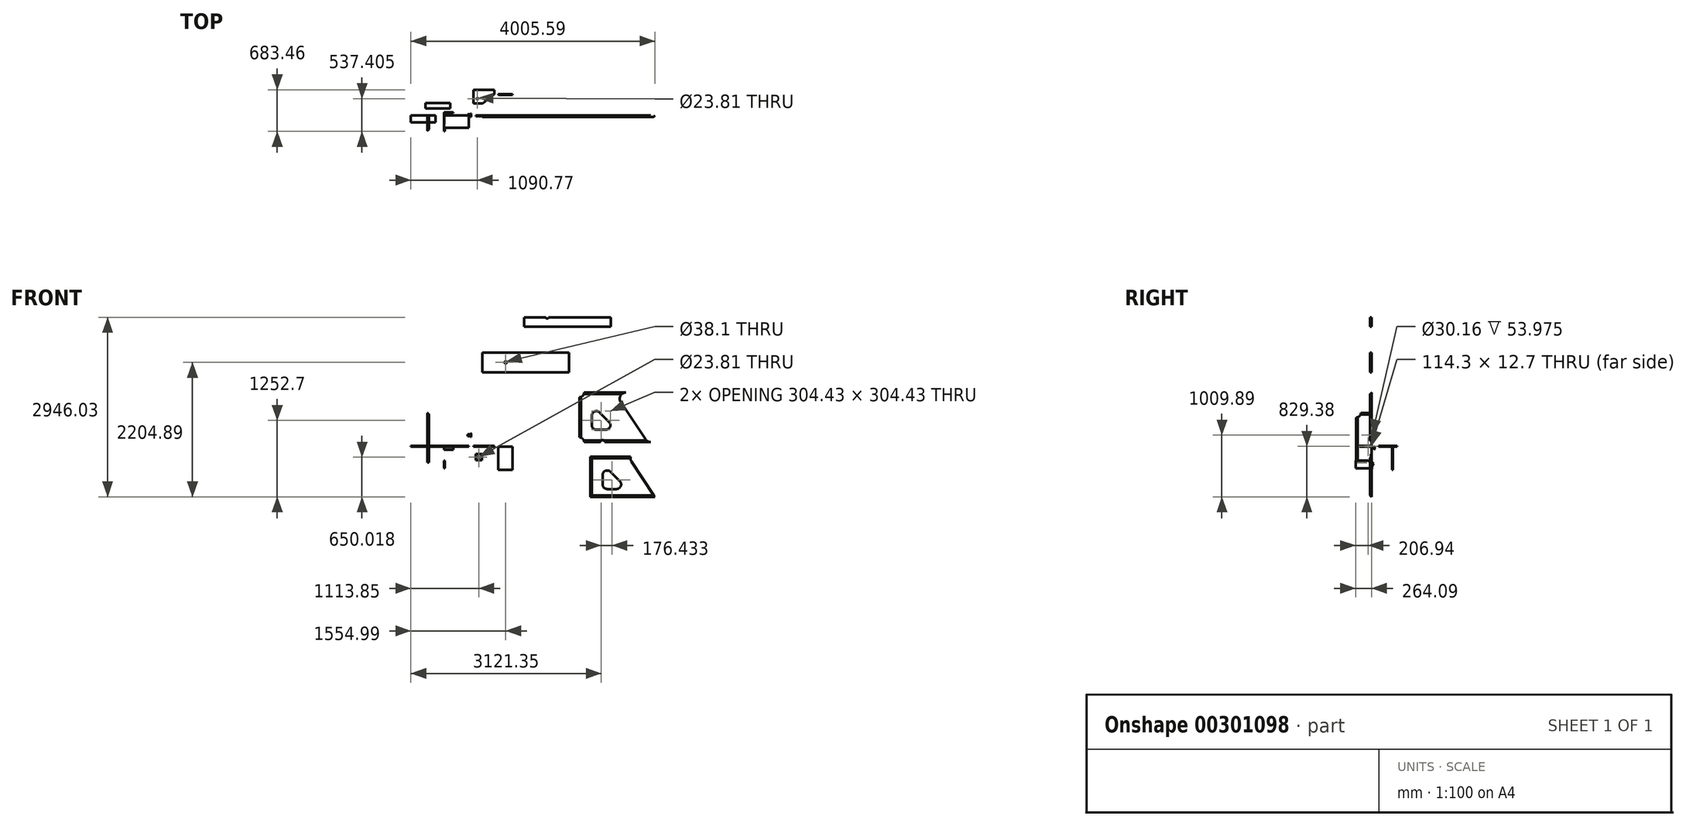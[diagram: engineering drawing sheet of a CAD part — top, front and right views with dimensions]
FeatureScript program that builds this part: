
annotation { "Feature Type Name" : "Feature", "Feature Type Description" : "" }
export const myFeature = defineFeature(function(context is Context, id is Id, definition is map)
    precondition{}
    {
        {
            var Q0;
            Q0=qCreatedBy(makeId("Top.planeOp"),FACE);
            var sketch = newSketch(context, id + "F0", { "sketchPlane" : qUnion([Q0])});
            skLineSegment(sketch, "E0.bottom", {"start": v(0, 0) * mm, "end": v(406.4, 0) * mm});
            skLineSegment(sketch, "E0.top", {"start": v(0, -203.2) * mm, "end": v(406.4, -203.2) * mm});
            skLineSegment(sketch, "E0.left", {"start": v(0, 0) * mm, "end": v(0, -203.2) * mm});
            skLineSegment(sketch, "E0.right", {"start": v(406.4, 0) * mm, "end": v(406.4, -203.2) * mm});
            skSolve(sketch);
        }
        {
            var Q0;
            Q0=makeQuery(id+"F0.imprint","IMPRINT",FACE,{"disambiguationData":[TD([[makeQuery(id+"F0.imprint","IMPRINT",EDGE,{"derivedFrom":sQuery(id+"F0.wireOp",EDGE,"E0.bottom")}),-1.0]])]});
            extrude(context, id + "F1", {"entities" : qUnion([Q0]), "depth" : 12.7 * mm});
        }
        {
            var Q0;
            Q0=makeQuery(id+"F1.opExtrude","SWEPT_FACE",FACE,{"disambiguationData":[OSD([sQuery(id+"F0.wireOp",EDGE,"E0.left")])]});
            var sketch = newSketch(context, id + "F2", { "sketchPlane" : qUnion([Q0])});
            skLineSegment(sketch, "E1", {"start": v(203.2, 12.7) * mm, "end": v(203.2, 0) * mm});
            skLineSegment(sketch, "E2", {"start": v(203.2, 0) * mm, "end": v(199.8, 0) * mm});
            skLineSegment(sketch, "E3", {"start": v(199.8, 0) * mm, "end": v(203.2, 12.7) * mm});
            skSolve(sketch);
        }
        {
            var Q0;
            Q0 = qSketchRegion(id + "F2", true);
            var Q1;
            Q1=makeQuery(id+"F1.opExtrude","SWEPT_BODY",BODY,{"disambiguationData":[OSD([sQuery(id+"F0.wireOp",EDGE,"E0.bottom"),sQuery(id+"F0.wireOp",EDGE,"E0.top"),sQuery(id+"F0.wireOp",EDGE,"E0.left"),sQuery(id+"F0.wireOp",EDGE,"E0.right")])]});
            extrude(context, id + "F3", {"entities" : qUnion([Q0]), "operationType" : NewBodyOperationType.REMOVE, "endBound" : BoundingType.UP_TO_BODY, "oppositeDirection" : true, "endBoundEntityBody" : qUnion([Q1]), "depth" : 25.4 * mm});
        }
        {
            var Q0;
            Q0=qCreatedBy(makeId("Top.planeOp"),FACE);
            var sketch = newSketch(context, id + "F4", { "sketchPlane" : qUnion([Q0])});
            skLineSegment(sketch, "E4.bottom", {"start": v(-140.72, 0) * mm, "end": v(-547.12, 0) * mm});
            skLineSegment(sketch, "E4.top", {"start": v(-140.72, -114.3) * mm, "end": v(-547.12, -114.3) * mm});
            skLineSegment(sketch, "E4.left", {"start": v(-140.72, 0) * mm, "end": v(-140.72, -114.3) * mm});
            skLineSegment(sketch, "E4.right", {"start": v(-547.12, 0) * mm, "end": v(-547.12, -114.3) * mm});
            skSolve(sketch);
        }
        {
            var Q0;
            Q0=makeQuery(id+"F4.imprint","IMPRINT",FACE,{"disambiguationData":[TD([[makeQuery(id+"F4.imprint","IMPRINT",EDGE,{"derivedFrom":sQuery(id+"F4.wireOp",EDGE,"E4.bottom")}),1.0]])]});
            extrude(context, id + "F5", {"entities" : qUnion([Q0]), "depth" : 12.7 * mm});
        }
        {
            var Q0;
            Q0=makeQuery(id+"F5.opExtrude","SWEPT_FACE",FACE,{"disambiguationData":[OSD([sQuery(id+"F4.wireOp",EDGE,"E4.right")])]});
            var sketch = newSketch(context, id + "F6", { "sketchPlane" : qUnion([Q0])});
            skLineSegment(sketch, "E5", {"start": v(0, 12.7) * mm, "end": v(0, 0) * mm});
            skLineSegment(sketch, "E6", {"start": v(0, 0) * mm, "end": v(3.4, 0) * mm});
            skLineSegment(sketch, "E7", {"start": v(3.4, 0) * mm, "end": v(0, 12.7) * mm});
            skSolve(sketch);
        }
        {
            var Q0;
            Q0 = qSketchRegion(id + "F6", true);
            extrude(context, id + "F7", {"entities" : qUnion([Q0]), "operationType" : NewBodyOperationType.REMOVE, "endBound" : BoundingType.THROUGH_ALL, "oppositeDirection" : true, "depth" : 25.4 * mm});
        }
        {
            var Q0;
            Q0=qCreatedBy(makeId("Top.planeOp"),FACE);
            var sketch = newSketch(context, id + "F8", { "sketchPlane" : qUnion([Q0])});
            skLineSegment(sketch, "E8.bottom", {"start": v(-305.25, 203.53) * mm, "end": v(101.15, 203.53) * mm});
            skLineSegment(sketch, "E8.top", {"start": v(-305.25, 114.63) * mm, "end": v(101.15, 114.63) * mm});
            skLineSegment(sketch, "E8.left", {"start": v(-305.25, 203.53) * mm, "end": v(-305.25, 114.63) * mm});
            skLineSegment(sketch, "E8.right", {"start": v(101.15, 203.53) * mm, "end": v(101.15, 114.63) * mm});
            skSolve(sketch);
        }
        {
            var Q0;
            Q0=makeQuery(id+"F8.imprint","IMPRINT",FACE,{"disambiguationData":[TD([[makeQuery(id+"F8.imprint","IMPRINT",EDGE,{"derivedFrom":sQuery(id+"F8.wireOp",EDGE,"E8.bottom")}),-1.0]])]});
            extrude(context, id + "F9", {"entities" : qUnion([Q0]), "depth" : 12.7 * mm});
        }
        {
            var Q0;
            Q0=qCreatedBy(makeId("Right.planeOp"),FACE);
            var sketch = newSketch(context, id + "F10", { "sketchPlane" : qUnion([Q0])});
            skLineSegment(sketch, "E9", {"start": v(-264.09, -226.14) * mm, "end": v(-64.29, -226.14) * mm});
            skLineSegment(sketch, "E10", {"start": v(-64.29, -226.14) * mm, "end": v(31.75, -281.59) * mm});
            skLineSegment(sketch, "E11", {"start": v(31.75, -281.59) * mm, "end": v(0, -336.58) * mm});
            skLineSegment(sketch, "E12", {"start": v(0, -336.58) * mm, "end": v(11, -342.93) * mm});
            skLineSegment(sketch, "E13", {"start": v(11, -342.93) * mm, "end": v(4.65, -353.93) * mm});
            skLineSegment(sketch, "E14", {"start": v(4.65, -353.93) * mm, "end": v(-264.09, -353.93) * mm});
            skLineSegment(sketch, "E15", {"start": v(-264.09, -353.93) * mm, "end": v(-264.09, -226.14) * mm});
            skSolve(sketch);
        }
        {
            var Q0;
            Q0=makeQuery(id+"F10.imprint","IMPRINT",FACE,{"disambiguationData":[TD([[makeQuery(id+"F10.imprint","IMPRINT",EDGE,{"derivedFrom":sQuery(id+"F10.wireOp",EDGE,"E9")}),-1.0]])]});
            extrude(context, id + "F11", {"entities" : qUnion([Q0]), "depth" : 12.7 * mm});
        }
        {
            var Q0;
            Q0=qCreatedBy(makeId("Right.planeOp"),FACE);
            var sketch = newSketch(context, id + "F12", { "sketchPlane" : qUnion([Q0])});
            skLineSegment(sketch, "E16.bottom", {"start": v(50.16, 0) * mm, "end": v(37.46, 0) * mm});
            skLineSegment(sketch, "E16.left", {"start": v(50.16, 0) * mm, "end": v(50.16, -38.1) * mm});
            skLineSegment(sketch, "E16.right", {"start": v(37.46, 0) * mm, "end": v(37.46, -50.8) * mm});
            skLineSegment(sketch, "E17", {"start": v(37.46, -50.8) * mm, "end": v(50.16, -38.1) * mm});
            skSolve(sketch);
        }
        {
            var Q0;
            Q0 = qSketchRegion(id + "F12", true);
            extrude(context, id + "F13", {"entities" : qUnion([Q0]), "depth" : 152.4 * mm});
        }
        {
            var Q0;
            Q0=qCreatedBy(makeId("Front.planeOp"),FACE);
            var sketch = newSketch(context, id + "F14", { "sketchPlane" : qUnion([Q0])});
            skLineSegment(sketch, "E18.bottom", {"start": v(-274.81, 553.7) * mm, "end": v(-249.41, 553.7) * mm});
            skLineSegment(sketch, "E18.top", {"start": v(-274.81, -259.1) * mm, "end": v(-249.41, -259.1) * mm});
            skLineSegment(sketch, "E18.left", {"start": v(-274.81, 553.7) * mm, "end": v(-274.81, -259.1) * mm});
            skLineSegment(sketch, "E18.right", {"start": v(-249.41, 553.7) * mm, "end": v(-249.41, -259.1) * mm});
            skSolve(sketch);
        }
        {
            var Q0;
            Q0 = qSketchRegion(id + "F14", true);
            extrude(context, id + "F15", {"entities" : qUnion([Q0]), "operationType" : NewBodyOperationType.ADD, "depth" : 254 * mm});
        }
        {
            var Q0;
            Q0=makeQuery(id+"F15.opExtrude","SWEPT_FACE",FACE,{"disambiguationData":[OSD([sQuery(id+"F14.wireOp",EDGE,"E18.right")])]});
            var sketch = newSketch(context, id + "F16", { "sketchPlane" : qUnion([Q0])});
            skCircle(sketch, "E19", {"center": v(-254, 553.7) * mm, "radius": 76.2 * mm});
            skSolve(sketch);
        }
        {
            var Q0;
            Q0 = qSketchRegion(id + "F16", true);
            extrude(context, id + "F17", {"entities" : qUnion([Q0]), "operationType" : NewBodyOperationType.REMOVE, "oppositeDirection" : true, "depth" : 25.4 * mm});
        }
        {
            var Q0;
            Q0=makeQuery(id+"F15.opExtrude","CAP_FACE",FACE,{"disambiguationData":[OSD([sQuery(id+"F14.wireOp",EDGE,"E18.bottom"),sQuery(id+"F14.wireOp",EDGE,"E18.top"),sQuery(id+"F14.wireOp",EDGE,"E18.left"),sQuery(id+"F14.wireOp",EDGE,"E18.right")])],"isStart":true});
            var sketch = newSketch(context, id + "F18", { "sketchPlane" : qUnion([Q0])});
            skLineSegment(sketch, "E20", {"start": v(274.81, 553.7) * mm, "end": v(249.41, 553.7) * mm});
            skLineSegment(sketch, "E21", {"start": v(249.41, 553.7) * mm, "end": v(249.41, 528.3) * mm});
            skLineSegment(sketch, "E22", {"start": v(249.41, 528.3) * mm, "end": v(274.81, 553.7) * mm});
            skSolve(sketch);
        }
        {
            var Q0;
            Q0 = qSketchRegion(id + "F18", true);
            extrude(context, id + "F19", {"entities" : qUnion([Q0]), "operationType" : NewBodyOperationType.REMOVE, "endBound" : BoundingType.UP_TO_NEXT, "oppositeDirection" : true, "depth" : 25.4 * mm});
        }
        {
            var Q0;
            Q0=makeQuery(id+"F15.opExtrude","SWEPT_FACE",FACE,{"disambiguationData":[OSD([sQuery(id+"F14.wireOp",EDGE,"E18.top")])]});
            var sketch = newSketch(context, id + "F20", { "sketchPlane" : qUnion([Q0])});
            skLineSegment(sketch, "E23", {"start": v(-274.81, 254) * mm, "end": v(-249.41, 254) * mm});
            skLineSegment(sketch, "E24", {"start": v(-249.41, 254) * mm, "end": v(-249.41, 228.6) * mm});
            skLineSegment(sketch, "E25", {"start": v(-249.41, 228.6) * mm, "end": v(-274.81, 254) * mm});
            skSolve(sketch);
        }
        {
            var Q0;
            Q0 = qSketchRegion(id + "F20", true);
            extrude(context, id + "F21", {"entities" : qUnion([Q0]), "operationType" : NewBodyOperationType.REMOVE, "endBound" : BoundingType.UP_TO_NEXT, "oppositeDirection" : true, "depth" : 25.4 * mm});
        }
        {
            var Q0;
            Q0=qCreatedBy(makeId("Front.planeOp"),FACE);
            var sketch = newSketch(context, id + "F22", { "sketchPlane" : qUnion([Q0])});
            skLineSegment(sketch, "E26", {"start": v(384.29, 203.53) * mm, "end": v(435.09, 203.53) * mm});
            skLineSegment(sketch, "E27", {"start": v(435.09, 203.53) * mm, "end": v(435.09, 215.44) * mm});
            skLineSegment(sketch, "E28", {"start": v(435.09, 215.44) * mm, "end": v(438.26, 215.44) * mm});
            skLineSegment(sketch, "E29", {"start": v(438.26, 215.44) * mm, "end": v(438.26, 201.95) * mm});
            skLineSegment(sketch, "E30", {"start": v(438.26, 201.95) * mm, "end": v(384.29, 201.95) * mm});
            skLineSegment(sketch, "E31", {"start": v(384.29, 201.95) * mm, "end": v(384.29, 203.53) * mm});
            skLineSegment(sketch, "E32", {"start": v(375.4, 186.86) * mm, "end": v(470.53, 186.86) * mm});
            skSolve(sketch);
        }
        {
            var Q0;
            Q0=makeQuery(id+"F22.imprint","IMPRINT",FACE,{"disambiguationData":[TD([[makeQuery(id+"F22.imprint","IMPRINT",EDGE,{"derivedFrom":sQuery(id+"F22.wireOp",EDGE,"E26")}),-1.0]])]});
            var Q1;
            Q1=sQuery(id+"F22.wireOp",EDGE,"E32");
            revolve(context, id + "F23", {"entities" : qUnion([Q0]), "axis" : qUnion([Q1]), "revolveType" : RevolveType.FULL});
        }
        {
            var Q0;
            Q0=qCreatedBy(makeId("Top.planeOp"),FACE);
            var sketch = newSketch(context, id + "F24", { "sketchPlane" : qUnion([Q0])});
            skLineSegment(sketch, "E33", {"start": v(480.15, 419.37) * mm, "end": v(823.05, 419.37) * mm});
            skLineSegment(sketch, "E34", {"start": v(823.05, 419.37) * mm, "end": v(823.05, 352.7) * mm});
            skLineSegment(sketch, "E35", {"start": v(820.67, 347.73) * mm, "end": v(632.55, 197.12) * mm});
            skLineSegment(sketch, "E36", {"start": v(632.55, 197.12) * mm, "end": v(480.15, 197.12) * mm});
            skLineSegment(sketch, "E37", {"start": v(480.15, 197.12) * mm, "end": v(480.15, 419.37) * mm});
            skPoint(sketch, "E38.visualSharp", {"position": v(823.05, 349.64) * mm});
            skArc(sketch, "E38.filletArc", {"start": v(820.67, 347.73) * mm, "mid": v(822.43, 349.94) * mm, "end": v(823.05, 352.7) * mm});
            skCircle(sketch, "E39", {"center": v(543.65, 273.32) * mm, "radius": 11.9 * mm});
            skSolve(sketch);
        }
        {
            var Q0;
            Q0 = qSketchRegion(id + "F24", true);
            extrude(context, id + "F25", {"entities" : qUnion([Q0]), "depth" : 12.7 * mm});
        }
        {
            var Q0;
            Q0=qCreatedBy(makeId("Top.planeOp"),FACE);
            var sketch = newSketch(context, id + "F26", { "sketchPlane" : qUnion([Q0])});
            skLineSegment(sketch, "E40.bottom", {"start": v(1123.97, 349.32) * mm, "end": v(888.39, 349.32) * mm});
            skLineSegment(sketch, "E40.top", {"start": v(1123.97, 336.62) * mm, "end": v(894.74, 336.62) * mm});
            skLineSegment(sketch, "E40.left", {"start": v(1123.97, 349.32) * mm, "end": v(1123.97, 336.62) * mm});
            skLineSegment(sketch, "E40.right", {"start": v(888.39, 349.32) * mm, "end": v(888.39, 342.97) * mm});
            skPoint(sketch, "E41.visualSharp", {"position": v(888.39, 336.62) * mm});
            skArc(sketch, "E41.filletArc", {"start": v(888.39, 342.97) * mm, "mid": v(890.25, 338.48) * mm, "end": v(894.74, 336.62) * mm});
            skSolve(sketch);
        }
        {
            var Q0;
            Q0 = qSketchRegion(id + "F26", true);
            extrude(context, id + "F27", {"entities" : qUnion([Q0]), "oppositeDirection" : true, "depth" : 381 * mm});
        }
        {
            var Q0;
            Q0=qCreatedBy(makeId("Front.planeOp"),FACE);
            var sketch = newSketch(context, id + "F28", { "sketchPlane" : qUnion([Q0])});
            skLineSegment(sketch, "E42.bottom", {"start": v(515.93, -122.21) * mm, "end": v(617.53, -122.21) * mm});
            skLineSegment(sketch, "E42.top", {"start": v(515.93, -223.81) * mm, "end": v(617.53, -223.81) * mm});
            skLineSegment(sketch, "E42.left", {"start": v(515.93, -122.21) * mm, "end": v(515.93, -223.81) * mm});
            skLineSegment(sketch, "E42.right", {"start": v(617.53, -122.21) * mm, "end": v(617.53, -223.81) * mm});
            skCircle(sketch, "E43", {"center": v(566.73, -173.01) * mm, "radius": 11.9 * mm});
            skSolve(sketch);
        }
        {
            var Q0;
            Q0 = qSketchRegion(id + "F28", true);
            extrude(context, id + "F29", {"entities" : qUnion([Q0]), "depth" : 12.7 * mm});
        }
        {
            var Q0;
            Q0=qCreatedBy(makeId("Front.planeOp"),FACE);
            var sketch = newSketch(context, id + "F30", { "sketchPlane" : qUnion([Q0])});
            skLineSegment(sketch, "E44.bottom", {"start": v(626.87, 1543.77) * mm, "end": v(2049.27, 1543.77) * mm});
            skLineSegment(sketch, "E44.top", {"start": v(626.87, 1219.95) * mm, "end": v(2049.27, 1219.95) * mm});
            skLineSegment(sketch, "E44.left", {"start": v(626.87, 1543.77) * mm, "end": v(626.87, 1219.95) * mm});
            skLineSegment(sketch, "E44.right", {"start": v(2049.27, 1543.77) * mm, "end": v(2049.27, 1219.95) * mm});
            skCircle(sketch, "E45", {"center": v(1007.87, 1381.86) * mm, "radius": 19.05 * mm});
            skLineSegment(sketch, "E46.bottom", {"start": v(1308.62, 2123) * mm, "end": v(1667.4, 2123) * mm});
            skLineSegment(sketch, "E46.left", {"start": v(1308.62, 2123) * mm, "end": v(1308.62, 1970.6) * mm});
            skLineSegment(sketch, "E46.right", {"start": v(2731.02, 2123) * mm, "end": v(2731.02, 1970.6) * mm});
            skLineSegment(sketch, "E47", {"start": v(2218.81, 810.85) * mm, "end": v(2218.81, 150.45) * mm});
            skLineSegment(sketch, "E48", {"start": v(2295.01, 74.25) * mm, "end": v(2564.89, 74.25) * mm});
            skLineSegment(sketch, "E49", {"start": v(2295.01, 887.05) * mm, "end": v(2980.81, 887.05) * mm});
            skLineSegment(sketch, "E50", {"start": v(2980.81, 887.05) * mm, "end": v(2980.81, 887.05) * mm});
            skArc(sketch, "E51", {"start": v(2218.81, 810.85) * mm, "mid": v(2272.7, 833.17) * mm, "end": v(2295.01, 887.05) * mm});
            skArc(sketch, "E52", {"start": v(2295.01, 74.25) * mm, "mid": v(2272.7, 128.13) * mm, "end": v(2218.81, 150.45) * mm});
            skArc(sketch, "E53", {"start": v(2552.1, 559.93) * mm, "mid": v(2469.05, 576.45) * mm, "end": v(2422.01, 506.05) * mm});
            skArc(sketch, "E54", {"start": v(2422.01, 353.65) * mm, "mid": v(2444.33, 299.77) * mm, "end": v(2498.21, 277.45) * mm});
            skArc(sketch, "E55", {"start": v(2650.61, 277.45) * mm, "mid": v(2721.01, 324.5) * mm, "end": v(2704.5, 407.53) * mm});
            skLineSegment(sketch, "E56", {"start": v(2498.21, 277.45) * mm, "end": v(2650.61, 277.45) * mm});
            skLineSegment(sketch, "E57", {"start": v(2422.01, 506.05) * mm, "end": v(2422.01, 353.65) * mm});
            skLineSegment(sketch, "E58", {"start": v(2552.1, 559.93) * mm, "end": v(2704.5, 407.53) * mm});
            skLineSegment(sketch, "E59.right", {"start": v(3302.68, 233.8) * mm, "end": v(3302.68, 232.2) * mm});
            skLineSegment(sketch, "E60", {"start": v(2896.28, 729.1) * mm, "end": v(3302.68, 119.5) * mm});
            skArc(sketch, "E61", {"start": v(3302.68, 119.5) * mm, "mid": v(3339.27, 86.27) * mm, "end": v(3387.21, 74.25) * mm});
            skArc(sketch, "E62", {"start": v(2980.81, 887.05) * mm, "mid": v(2891.24, 833.4) * mm, "end": v(2896.28, 729.1) * mm});
            skPoint(sketch, "E63", {"position": v(1308.62, 2046.8) * mm});
            skPoint(sketch, "E64", {"position": v(626.87, 1381.86) * mm});
            skArc(sketch, "E65", {"start": v(2634.74, 74.25) * mm, "mid": v(2599.81, 109.18) * mm, "end": v(2564.89, 74.25) * mm});
            skLineSegment(sketch, "E66.trimOffspring", {"start": v(2634.74, 74.25) * mm, "end": v(3387.21, 74.25) * mm});
            skLineSegment(sketch, "E67.trimOffspring", {"start": v(1308.62, 1970.6) * mm, "end": v(2731.02, 1970.6) * mm});
            skArc(sketch, "E68", {"start": v(1667.4, 2123) * mm, "mid": v(1689.62, 2100.77) * mm, "end": v(1711.85, 2123) * mm});
            skLineSegment(sketch, "E69.trimOffspring", {"start": v(1711.85, 2123) * mm, "end": v(2731.02, 2123) * mm});
            skSolve(sketch);
        }
        {
            var Q0;
            Q0 = qSketchRegion(id + "F30", true);
            extrude(context, id + "F31", {"entities" : qUnion([Q0]), "depth" : 25.4 * mm});
        }
        {
            var Q0;
            Q0=makeQuery(id+"F31.opExtrude","CAP_EDGE",EDGE,{"disambiguationData":[OSD([sQuery(id+"F30.wireOp",EDGE,"E49")])],"isStart":false});
            var Q1;
            Q1=makeQuery(id+"F31.opExtrude","CAP_EDGE",EDGE,{"disambiguationData":[OSD([sQuery(id+"F30.wireOp",EDGE,"E48")])],"isStart":false});
            var Q2;
            Q2=makeQuery(id+"F31.opExtrude","CAP_EDGE",EDGE,{"disambiguationData":[OSD([sQuery(id+"F30.wireOp",EDGE,"E47")])],"isStart":false});
            var Q3;
            Q3=makeQuery(id+"F31.opExtrude","CAP_EDGE",EDGE,{"disambiguationData":[OSD([sQuery(id+"F30.wireOp",EDGE,"E66.trimOffspring")])],"isStart":false});
            chamfer(context, id + "F32", {"entities" : qUnion([Q0, Q1, Q2, Q3]), "width" : 25.4 * mm, "tangentPropagation" : true});
        }
        {
            var Q0;
            Q0=qCreatedBy(makeId("Front.planeOp"),FACE);
            var sketch = newSketch(context, id + "F33", { "sketchPlane" : qUnion([Q0])});
            skLineSegment(sketch, "E70", {"start": v(2395.25, -162.63) * mm, "end": v(2395.25, -823.03) * mm});
            skLineSegment(sketch, "E71", {"start": v(784.89, -86.43) * mm, "end": v(784.89, -86.43) * mm});
            skArc(sketch, "E72", {"start": v(2728.53, -413.55) * mm, "mid": v(2645.49, -397.03) * mm, "end": v(2598.45, -467.43) * mm});
            skArc(sketch, "E73", {"start": v(2598.45, -619.83) * mm, "mid": v(2620.77, -673.71) * mm, "end": v(2674.65, -696.03) * mm});
            skArc(sketch, "E74", {"start": v(2827.05, -696.03) * mm, "mid": v(2897.45, -649) * mm, "end": v(2880.93, -565.95) * mm});
            skLineSegment(sketch, "E75", {"start": v(2674.65, -696.03) * mm, "end": v(2827.05, -696.03) * mm});
            skLineSegment(sketch, "E76", {"start": v(2598.45, -467.43) * mm, "end": v(2598.45, -619.83) * mm});
            skLineSegment(sketch, "E77", {"start": v(2728.53, -413.55) * mm, "end": v(2880.93, -565.95) * mm});
            skLineSegment(sketch, "E78", {"start": v(3072.71, -244.39) * mm, "end": v(3458.47, -823.03) * mm});
            skArc(sketch, "E79", {"start": v(3058.87, -162.63) * mm, "mid": v(3057.07, -204.99) * mm, "end": v(3072.71, -244.39) * mm});
            skLineSegment(sketch, "E80", {"start": v(2395.25, -162.63) * mm, "end": v(3058.87, -162.63) * mm});
            skLineSegment(sketch, "E81", {"start": v(2395.25, -823.03) * mm, "end": v(3458.47, -823.03) * mm});
            skSolve(sketch);
        }
        {
            var Q0;
            Q0 = qSketchRegion(id + "F33", true);
            extrude(context, id + "F34", {"entities" : qUnion([Q0]), "depth" : 25.4 * mm, "offsetDistance" : 25.4 * mm});
        }
        {
            var Q0;
            Q0=makeQuery(id+"F34.opExtrude","CAP_EDGE",EDGE,{"disambiguationData":[OSD([sQuery(id+"F33.wireOp",EDGE,"E80")])],"isStart":false});
            var Q1;
            Q1=makeQuery(id+"F34.opExtrude","CAP_EDGE",EDGE,{"disambiguationData":[OSD([sQuery(id+"F33.wireOp",EDGE,"E70")])],"isStart":false});
            var Q2;
            Q2=makeQuery(id+"F34.opExtrude","CAP_EDGE",EDGE,{"disambiguationData":[OSD([sQuery(id+"F33.wireOp",EDGE,"E81")])],"isStart":false});
            chamfer(context, id + "F35", {"entities" : qUnion([Q0, Q1, Q2]), "width" : 25.4 * mm, "tangentPropagation" : true});
        }
    });
